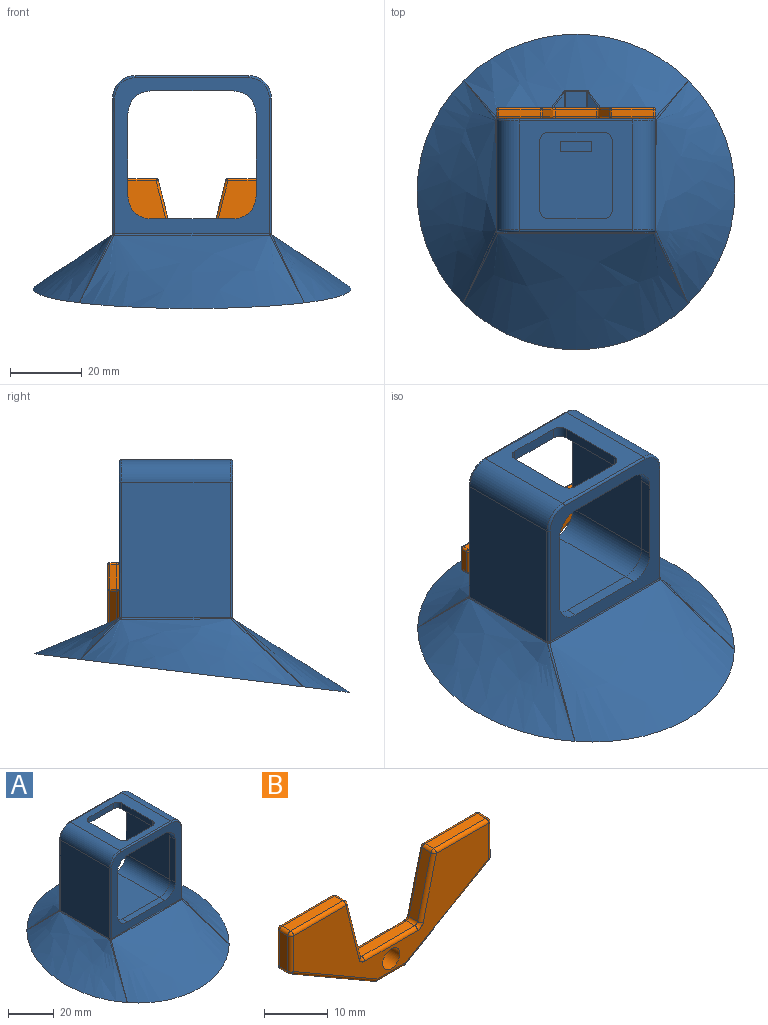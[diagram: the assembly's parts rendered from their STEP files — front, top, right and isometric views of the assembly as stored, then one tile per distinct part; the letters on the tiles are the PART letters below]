
ASSEMBLY  parts=2 mates=1
PART A: 88 faces, bbox 88.9x88.3x65.7 mm
  f0: plane 28.45x25.65mm, normal (0,0,1), area 705.5mm2, adj f4,f14,f20,f21,f79,f80,f81,f82
  f1: bspline ~21.48x0.61mm, area 7.3mm2, adj f4,f33,f65,f78
  f2: plane 31.75x30.48mm, normal (0,0,1), area 483mm2, adj f23,f24,f25,f26,f27,f28,f29,f30
  f3: plane 28.45x25.65mm, normal (0,0,-1), area 245mm2, adj f4,f14,f19,f22,f25,f26,f27,f28
  f4: plane 47.12x43.18mm, normal (0,1,0), area 462.5mm2, adj f0,f1,f3,f12,f13,f19,f20,f21
  f5: plane 43.54x43.18mm, normal (0,-1,0), area 615.7mm2, adj f8,f9,f10,f11,f15,f16,f17,f18
  f6: plane 37.94x30.48mm, normal (1,0,0), area 1152.3mm2, adj f24,f43,f45,f58
  f7: plane 37.94x30.48mm, normal (-1,0,0), area 1152.3mm2, adj f23,f38,f50,f59
  f8: plane 23.11x3.3mm, normal (-1,0,0), area 76.3mm2, adj f5,f14,f15,f18
  f9: plane 23.11x3.3mm, normal (0,0,1), area 76.3mm2, adj f5,f14,f15,f16
  f10: plane 23.11x3.3mm, normal (1,0,0), area 76.3mm2, adj f5,f14,f16,f17
  f11: plane 23.11x3.3mm, normal (0,0,-1), area 76.3mm2, adj f5,f14,f17,f18
  f12: plane 28.45x25.65mm, normal (1,0,0), area 729.8mm2, adj f4,f14,f19,f20
  f13: plane 28.45x25.65mm, normal (-1,0,0), area 729.8mm2, adj f4,f14,f21,f22
  f14: plane 38.35x38.35mm, normal (0,1,0), area 188.4mm2, adj f0,f3,f8,f9,f10,f11,f12,f13
  f15: cylinder r=6.35mm len=6.35mm, axis (0,1,0), area 32.9mm2, adj f5,f8,f9,f14
  f16: cylinder r=6.35mm len=6.35mm, axis (0,-1,0), area 32.9mm2, adj f5,f9,f10,f14
  f17: cylinder r=6.35mm len=6.35mm, axis (0,1,0), area 32.9mm2, adj f5,f10,f11,f14
  f18: cylinder r=6.35mm len=6.35mm, axis (0,-1,0), area 32.9mm2, adj f5,f8,f11,f14
  f19: cylinder r=6.35mm len=28.45mm, axis (0,-1,0), area 283.8mm2, adj f3,f4,f12,f14
  f20: cylinder r=6.35mm len=28.45mm, axis (0,1,0), area 283.8mm2, adj f0,f4,f12,f14
  f21: cylinder r=6.35mm len=28.45mm, axis (0,-1,0), area 283.8mm2, adj f0,f4,f13,f14
  f22: cylinder r=6.35mm len=28.45mm, axis (0,1,0), area 283.8mm2, adj f3,f4,f13,f14
  f23: cylinder r=6.35mm len=30.48mm, axis (0,1,0), area 304mm2, adj f2,f7,f39,f48
  f24: cylinder r=6.35mm len=30.48mm, axis (0,-1,0), area 304mm2, adj f2,f6,f41,f46
  f25: plane 19.05x3.05mm, normal (-1,0,0), area 58.1mm2, adj f2,f3,f29,f31
  f26: plane 15.24x3.05mm, normal (0,-1,0), area 46.5mm2, adj f2,f3,f29,f30
  f27: plane 19.05x3.05mm, normal (1,0,0), area 58.1mm2, adj f2,f3,f30,f32
  f28: plane 15.24x3.05mm, normal (0,1,0), area 46.5mm2, adj f2,f3,f31,f32
  f29: cylinder r=2.54mm len=3.05mm, axis (0,0,1), area 12.2mm2, adj f2,f3,f25,f26
  f30: cylinder r=2.54mm len=3.05mm, axis (0,0,-1), area 12.2mm2, adj f2,f3,f26,f27
  f31: cylinder r=2.54mm len=3.05mm, axis (0,0,-1), area 12.2mm2, adj f2,f3,f25,f28
  f32: cylinder r=2.54mm len=3.05mm, axis (0,0,1), area 12.2mm2, adj f2,f3,f27,f28
  f33: bspline ~62.86x23.73mm, area 1159.6mm2, adj f1,f37,f42,f64,f65,f66,f73,f74
  f34: bspline ~62.39x22.23mm, area 1231.2mm2, adj f37,f49,f57,f59,f61,f87
  f35: bspline ~62.86x32.77mm, area 1957mm2, adj f44,f49,f51,f52,f53,f87
  f36: bspline ~62.39x22.23mm, area 1232.3mm2, adj f42,f44,f56,f58,f60,f87
  f37: bspline ~12.59x12.34mm, area 3.4mm2, adj f33,f34,f63
  f38: cylinder r=0.64mm len=37.86mm, axis (0,0,-1), area 37.7mm2, adj f4,f7,f39,f61,f63,f65
  f39: torus R=5.71mm, axis (0,-1,0), area 9.6mm2, adj f4,f23,f38,f40
  f40: cylinder r=0.64mm len=31.75mm, axis (1,0,0), area 31.7mm2, adj f2,f4,f39,f41
  f41: torus R=5.71mm, axis (0,-1,0), area 9.6mm2, adj f4,f24,f40,f43
  f42: bspline ~12.89x12.45mm, area 3.4mm2, adj f33,f36,f62
  f43: cylinder r=0.64mm len=37.86mm, axis (0,0,1), area 37.7mm2, adj f4,f6,f41,f60,f62,f64
  f44: bspline ~22.84x21.53mm, area 6mm2, adj f35,f36,f54
  f45: cylinder r=0.64mm len=37.94mm, axis (0,0,-1), area 37.7mm2, adj f5,f6,f46,f52,f54,f56
  f46: torus R=5.71mm, axis (0,-1,0), area 9.6mm2, adj f5,f24,f45,f47
  f47: cylinder r=0.64mm len=31.75mm, axis (-1,0,0), area 31.7mm2, adj f2,f5,f46,f48
  f48: torus R=5.71mm, axis (0,-1,0), area 9.6mm2, adj f5,f23,f47,f50
  f49: bspline ~22.27x21.15mm, area 6mm2, adj f34,f35,f55
  f50: cylinder r=0.64mm len=37.94mm, axis (0,0,1), area 37.7mm2, adj f5,f7,f48,f53,f55,f57
  f51: bspline ~50.51x0.54mm, area 26.1mm2, adj f5,f35,f52,f53
  f52: bspline ~0.55x0.5mm, area 0.1mm2, adj f35,f45,f51,f54
  f53: bspline ~0.55x0.55mm, area 0.1mm2, adj f35,f50,f51,f55
  f54: bspline ~0.81x0.61mm, area 0.4mm2, adj f44,f45,f52,f56
  f55: bspline ~0.75x0.71mm, area 0.4mm2, adj f49,f50,f53,f57
  f56: bspline ~0.38x0.36mm, area 0mm2, adj f36,f45,f54,f58
  f57: bspline ~0.37x0.34mm, area 0mm2, adj f34,f50,f55,f59
  f58: bspline ~34.03x0.53mm, area 16.8mm2, adj f6,f36,f56,f60
  f59: bspline ~35.85x0.53mm, area 16.8mm2, adj f7,f34,f57,f61
  f60: bspline ~0.59x0.48mm, area 0.1mm2, adj f36,f43,f58,f62
  f61: bspline ~0.58x0.55mm, area 0.1mm2, adj f34,f38,f59,f63
  f62: bspline ~0.74x0.67mm, area 0.4mm2, adj f42,f43,f60,f64
  f63: bspline ~0.78x0.63mm, area 0.4mm2, adj f37,f38,f61,f65
  f64: bspline ~0.61x0.57mm, area 0.1mm2, adj f33,f43,f62,f66
  f65: bspline ~0.62x0.51mm, area 0.1mm2, adj f1,f33,f38,f63
  f66: bspline ~21.93x0.62mm, area 7.3mm2, adj f4,f33,f64,f72
  f67: plane 7.3x5.48mm, normal (-0.49,0,0.87), area 22.3mm2, adj f4,f70,f72,f73
  f68: plane 7.8x6.02mm, normal (0,0,1), area 46.8mm2, adj f4,f70,f71,f75
  f69: plane 7.31x5.48mm, normal (0.49,0,0.87), area 22.4mm2, adj f4,f71,f77,f78
  f70: cylinder r=0.64mm len=7.72mm, axis (0,-1,0), area 2.4mm2, adj f4,f67,f68,f74
  f71: cylinder r=0.64mm len=7.73mm, axis (0,1,0), area 2.4mm2, adj f4,f68,f69,f76
  f72: bspline ~2.97x1.49mm, area 0.4mm2, adj f4,f66,f67,f73
  f73: bspline ~12.76x9.78mm, area 4mm2, adj f33,f67,f72,f74
  f74: bspline ~0.92x0.9mm, area 0.2mm2, adj f33,f70,f73,f75
  f75: bspline ~18.33x0.94mm, area 1.5mm2, adj f33,f68,f74,f76
  f76: bspline ~0.92x0.9mm, area 0.2mm2, adj f33,f71,f75,f77
  f77: bspline ~12.76x9.78mm, area 4mm2, adj f33,f69,f76,f78
  f78: bspline ~2.72x1.35mm, area 0.4mm2, adj f1,f4,f69,f77
  f79: plane 6.35x2.78mm, normal (-1,0,0), area 17.6mm2, adj f0,f80,f82,f83
  f80: plane 8.73x6.35mm, normal (0,-1,0), area 44.1mm2, adj f0,f79,f81,f83,f86
  f81: plane 6.35x2.78mm, normal (1,0,0), area 17.6mm2, adj f0,f80,f82,f83
  f82: plane 8.73x6.35mm, normal (0,1,0), area 44.1mm2, adj f0,f79,f81,f83,f84
  f83: plane 8.73x2.78mm, normal (0,0,1), area 24.3mm2, adj f79,f80,f81,f82
  f84: cylinder r=1.9mm len=3.8mm, axis (0,1,0), area 42.6mm2, adj f82,f85
  f85: cone r=0mm half-angle=59deg, axis (0,1,0), area 13.2mm2, adj f84
  f86: cylinder r=1.9mm len=6.35mm, axis (0,1,0), area 75.8mm2, adj f4,f80
  f87: sphere r=241.3mm, area 6260.8mm2, adj f33,f34,f35,f36
PART B: 63 faces, bbox 44.5x3.2x18.8 mm
  f0: plane 11.74x2.93mm, normal (0.97,0,0.24), area 23mm2, adj f50,f55,f58,f61
  f1: plane 11.57x1.91mm, normal (0,0,1), area 22mm2, adj f47,f56,f57,f61
  f2: plane 6.8x1.91mm, normal (-1,0,0), area 12.9mm2, adj f37,f46,f47,f48
  f3: plane 18.59x10.73mm, normal (-0.5,0,-0.87), area 40.9mm2, adj f27,f36,f37,f38
  f4: plane 6.01x1.91mm, normal (0,0,-1), area 11.4mm2, adj f17,f26,f27,f28
  f5: plane 18.59x10.73mm, normal (0.5,0,-0.87), area 40.9mm2, adj f12,f16,f17,f18
  f6: plane 6.8x1.91mm, normal (1,0,0), area 12.9mm2, adj f12,f15,f19,f20
  f7: plane 11.57x1.91mm, normal (0,0,1), area 22mm2, adj f20,f25,f29,f30
  f8: plane 11.74x2.93mm, normal (-0.97,0,0.24), area 23mm2, adj f30,f35,f39,f40
  f9: plane 11.71x1.91mm, normal (0,0,1), area 22.3mm2, adj f40,f45,f49,f50
  f10: plane 43.18x17.53mm, normal (0,-1,0), area 332.2mm2, adj f15,f16,f25,f26,f35,f36,f41,f45
  f11: plane 43.18x17.53mm, normal (0,1,0), area 332.2mm2, adj f18,f19,f28,f29,f38,f39,f44,f48
  f12: cylinder r=0.64mm len=1.91mm, axis (0,1,0), area 1.3mm2, adj f5,f6,f13,f14
  f13: sphere r=0.64mm, area 0.4mm2, adj f12,f15,f16
  f14: sphere r=0.64mm, area 0.4mm2, adj f12,f18,f19
  f15: cylinder r=0.64mm len=6.8mm, axis (0,0,-1), area 6.8mm2, adj f6,f10,f13,f21
  f16: cylinder r=0.64mm len=18.9mm, axis (-0.87,0,-0.5), area 21.4mm2, adj f5,f10,f13,f22
  f17: cylinder r=0.64mm len=1.91mm, axis (0,1,0), area 0.6mm2, adj f4,f5,f22,f23
  f18: cylinder r=0.64mm len=18.9mm, axis (0.87,0,0.5), area 21.4mm2, adj f5,f11,f14,f23
  f19: cylinder r=0.64mm len=6.8mm, axis (0,0,1), area 6.8mm2, adj f6,f11,f14,f24
  f20: cylinder r=0.64mm len=1.91mm, axis (0,-1,0), area 1.9mm2, adj f6,f7,f21,f24
  f21: sphere r=0.64mm, area 0.6mm2, adj f15,f20,f25
  f22: sphere r=0.64mm, area 0.2mm2, adj f16,f17,f26
  f23: sphere r=0.64mm, area 0.2mm2, adj f17,f18,f28
  f24: sphere r=0.64mm, area 0.6mm2, adj f19,f20,f29
  f25: cylinder r=0.64mm len=11.57mm, axis (1,0,0), area 11.5mm2, adj f7,f10,f21,f31
  f26: cylinder r=0.64mm len=6.01mm, axis (-1,0,0), area 6mm2, adj f4,f10,f22,f32
  f27: cylinder r=0.64mm len=1.91mm, axis (0,1,0), area 0.6mm2, adj f3,f4,f32,f33
  f28: cylinder r=0.64mm len=6.01mm, axis (1,0,0), area 6mm2, adj f4,f11,f23,f33
  f29: cylinder r=0.64mm len=11.57mm, axis (-1,0,0), area 11.5mm2, adj f7,f11,f24,f34
  f30: cylinder r=0.64mm len=1.91mm, axis (0,1,0), area 1.6mm2, adj f7,f8,f31,f34
  f31: sphere r=0.64mm, area 0.5mm2, adj f25,f30,f35
  f32: sphere r=0.64mm, area 0.2mm2, adj f26,f27,f36
  f33: sphere r=0.64mm, area 0.2mm2, adj f27,f28,f38
  f34: sphere r=0.64mm, area 0.5mm2, adj f29,f30,f39
  f35: cylinder r=0.64mm len=11.89mm, axis (0.24,0,0.97), area 12.1mm2, adj f8,f10,f31,f41
  f36: cylinder r=0.64mm len=18.9mm, axis (-0.87,0,0.5), area 21.4mm2, adj f3,f10,f32,f42
  f37: cylinder r=0.64mm len=1.91mm, axis (0,1,0), area 1.3mm2, adj f2,f3,f42,f43
  f38: cylinder r=0.64mm len=18.9mm, axis (0.87,0,-0.5), area 21.4mm2, adj f3,f11,f33,f43
  f39: cylinder r=0.64mm len=11.89mm, axis (-0.24,0,-0.97), area 12.1mm2, adj f8,f11,f34,f44
  f40: cylinder r=0.64mm len=1.91mm, axis (0,1,0), area 1.6mm2, adj f8,f9,f41,f44
  f41: torus R=1.27mm, axis (0,-1,0), area 1.1mm2, adj f10,f35,f40,f45
  f42: sphere r=0.64mm, area 0.4mm2, adj f36,f37,f46
  f43: sphere r=0.64mm, area 0.4mm2, adj f37,f38,f48
  f44: torus R=1.27mm, axis (0,-1,0), area 1.1mm2, adj f11,f39,f40,f49
  f45: cylinder r=0.64mm len=11.71mm, axis (1,0,0), area 11.7mm2, adj f9,f10,f41,f51
  f46: cylinder r=0.64mm len=6.8mm, axis (0,0,1), area 6.8mm2, adj f2,f10,f42,f52
  f47: cylinder r=0.64mm len=1.91mm, axis (0,1,0), area 1.9mm2, adj f1,f2,f52,f53
  f48: cylinder r=0.64mm len=6.8mm, axis (0,0,-1), area 6.8mm2, adj f2,f11,f43,f53
  f49: cylinder r=0.64mm len=11.71mm, axis (-1,0,0), area 11.7mm2, adj f9,f11,f44,f54
  f50: cylinder r=0.64mm len=1.91mm, axis (0,-1,0), area 1.6mm2, adj f0,f9,f51,f54
  f51: torus R=1.27mm, axis (0,-1,0), area 1.1mm2, adj f10,f45,f50,f55
  f52: sphere r=0.64mm, area 0.6mm2, adj f46,f47,f56
  f53: sphere r=0.64mm, area 0.6mm2, adj f47,f48,f57
  f54: torus R=1.27mm, axis (0,-1,0), area 1.1mm2, adj f11,f49,f50,f58
  f55: cylinder r=0.64mm len=11.89mm, axis (0.24,0,-0.97), area 12.1mm2, adj f0,f10,f51,f59
  f56: cylinder r=0.64mm len=11.57mm, axis (1,0,0), area 11.5mm2, adj f1,f10,f52,f59
  f57: cylinder r=0.64mm len=11.57mm, axis (-1,0,0), area 11.5mm2, adj f1,f11,f53,f60
  f58: cylinder r=0.64mm len=11.89mm, axis (-0.24,0,0.97), area 12.1mm2, adj f0,f11,f54,f60
  f59: sphere r=0.64mm, area 0.5mm2, adj f55,f56,f61
  f60: sphere r=0.64mm, area 0.5mm2, adj f57,f58,f61
  f61: cylinder r=0.64mm len=1.91mm, axis (0,1,0), area 1.6mm2, adj f0,f1,f59,f60
  f62: cylinder r=1.9mm len=3.8mm, axis (0,1,0), area 37.9mm2, adj f10,f11
PLACE A t=(0,0,-0.25)mm
PLACE B t=(0,19.05,-3.43)mm
MATE fastened B.f62 <-> A.f84  axis (0,-1,0) through (0,15.88,-0.38)mm
